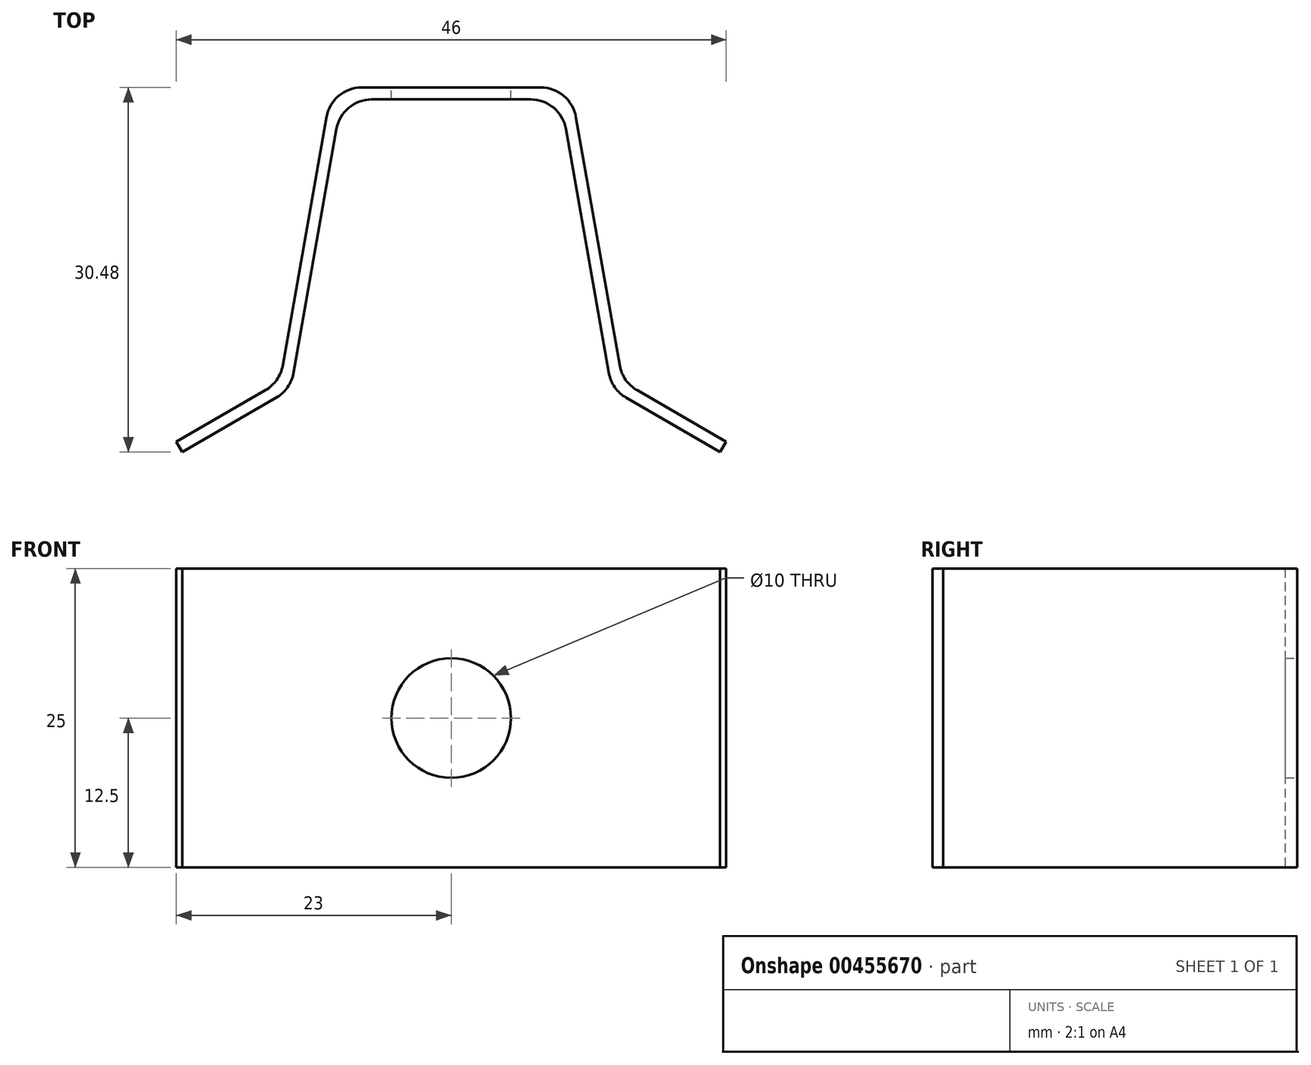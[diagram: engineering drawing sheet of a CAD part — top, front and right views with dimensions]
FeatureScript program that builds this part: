
annotation { "Feature Type Name" : "Feature", "Feature Type Description" : "" }
export const myFeature = defineFeature(function(context is Context, id is Id, definition is map)
    precondition{}
    {
        {
            var Q0;
            Q0=qCreatedBy(makeId("Top.planeOp"),FACE);
            var sketch = newSketch(context, id + "F0", { "sketchPlane" : qUnion([Q0])});
            skLineSegment(sketch, "E0", {"start": v(0, 22.98) * mm, "end": v(-7.48, 22.98) * mm});
            skLineSegment(sketch, "E1", {"start": v(-10.44, 20.5) * mm, "end": v(-14.1, -0.26) * mm});
            skLineSegment(sketch, "E2", {"start": v(-15.55, -2.34) * mm, "end": v(-23, -6.64) * mm});
            skLineSegment(sketch, "E3", {"start": v(-23, -6.64) * mm, "end": v(-22.5, -7.5) * mm});
            skLineSegment(sketch, "E4", {"start": v(-22.5, -7.5) * mm, "end": v(-14.65, -2.97) * mm});
            skLineSegment(sketch, "E5", {"start": v(-13.2, -0.9) * mm, "end": v(-9.6, 19.5) * mm});
            skLineSegment(sketch, "E6", {"start": v(-6.64, 21.98) * mm, "end": v(0, 21.98) * mm});
            skLineSegment(sketch, "E7.MirrorCS", {"start": v(23, -6.64) * mm, "end": v(22.5, -7.5) * mm});
            skLineSegment(sketch, "E8.MirrorCS", {"start": v(0, 22.98) * mm, "end": v(7.48, 22.98) * mm});
            skLineSegment(sketch, "E9.MirrorCS", {"start": v(22.5, -7.5) * mm, "end": v(14.65, -2.97) * mm});
            skLineSegment(sketch, "E10.MirrorCS", {"start": v(6.64, 21.98) * mm, "end": v(0, 21.98) * mm});
            skLineSegment(sketch, "E11.MirrorCS", {"start": v(15.55, -2.34) * mm, "end": v(23, -6.64) * mm});
            skLineSegment(sketch, "E12.MirrorCS", {"start": v(10.44, 20.5) * mm, "end": v(14.1, -0.26) * mm});
            skLineSegment(sketch, "E13.MirrorCS", {"start": v(13.2, -0.9) * mm, "end": v(9.6, 19.5) * mm});
            skPoint(sketch, "E14.visualSharp", {"position": v(-10, 22.98) * mm});
            skArc(sketch, "E14.filletArc", {"start": v(-7.48, 22.98) * mm, "mid": v(-9.41, 22.28) * mm, "end": v(-10.44, 20.5) * mm});
            skPoint(sketch, "E15.visualSharp", {"position": v(-9.16, 21.98) * mm});
            skArc(sketch, "E15.filletArc", {"start": v(-6.64, 21.98) * mm, "mid": v(-8.57, 21.28) * mm, "end": v(-9.6, 19.5) * mm});
            skPoint(sketch, "E16.visualSharp", {"position": v(-13.44, -2.27) * mm});
            skArc(sketch, "E16.filletArc", {"start": v(-14.65, -2.97) * mm, "mid": v(-13.7, -2.1) * mm, "end": v(-13.2, -0.9) * mm});
            skPoint(sketch, "E17.visualSharp", {"position": v(-14.34, -1.64) * mm});
            skArc(sketch, "E17.filletArc", {"start": v(-15.55, -2.34) * mm, "mid": v(-14.6, -1.46) * mm, "end": v(-14.1, -0.26) * mm});
            skPoint(sketch, "E18.visualSharp", {"position": v(13.44, -2.27) * mm});
            skArc(sketch, "E18.filletArc", {"start": v(13.2, -0.9) * mm, "mid": v(13.7, -2.1) * mm, "end": v(14.65, -2.97) * mm});
            skPoint(sketch, "E19.visualSharp", {"position": v(14.34, -1.64) * mm});
            skArc(sketch, "E19.filletArc", {"start": v(14.1, -0.26) * mm, "mid": v(14.6, -1.46) * mm, "end": v(15.55, -2.34) * mm});
            skPoint(sketch, "E20.visualSharp", {"position": v(10, 22.98) * mm});
            skArc(sketch, "E20.filletArc", {"start": v(10.44, 20.5) * mm, "mid": v(9.41, 22.28) * mm, "end": v(7.48, 22.98) * mm});
            skPoint(sketch, "E21.visualSharp", {"position": v(9.16, 21.98) * mm});
            skArc(sketch, "E21.filletArc", {"start": v(9.6, 19.5) * mm, "mid": v(8.57, 21.28) * mm, "end": v(6.64, 21.98) * mm});
            skSolve(sketch);
        }
        {
            var Q0;
            Q0 = qSketchRegion(id + "F0", true);
            extrude(context, id + "F1", {"entities" : qUnion([Q0]), "depth" : 25 * mm});
        }
        {
            var Q0;
            Q0=makeQuery(id+"F1.opExtrude","SWEPT_FACE",FACE,{"disambiguationData":[OSD([sQuery(id+"F0.wireOp",EDGE,"E0"),sQuery(id+"F0.wireOp",EDGE,"E8.MirrorCS")])]});
            var sketch = newSketch(context, id + "F2", { "sketchPlane" : qUnion([Q0])});
            skCircle(sketch, "E22", {"center": v(0, 12.5) * mm, "radius": 5 * mm});
            skSolve(sketch);
        }
        {
            var Q0;
            Q0=makeQuery(id+"F2.imprint","IMPRINT",FACE,{"disambiguationData":[TD([[makeQuery(id+"F2.imprint","IMPRINT",EDGE,{"derivedFrom":sQuery(id+"F2.wireOp",EDGE,"E22")}),1.0]])]});
            extrude(context, id + "F3", {"entities" : qUnion([Q0]), "operationType" : NewBodyOperationType.REMOVE, "oppositeDirection" : true, "depth" : 25 * mm});
        }
    });
